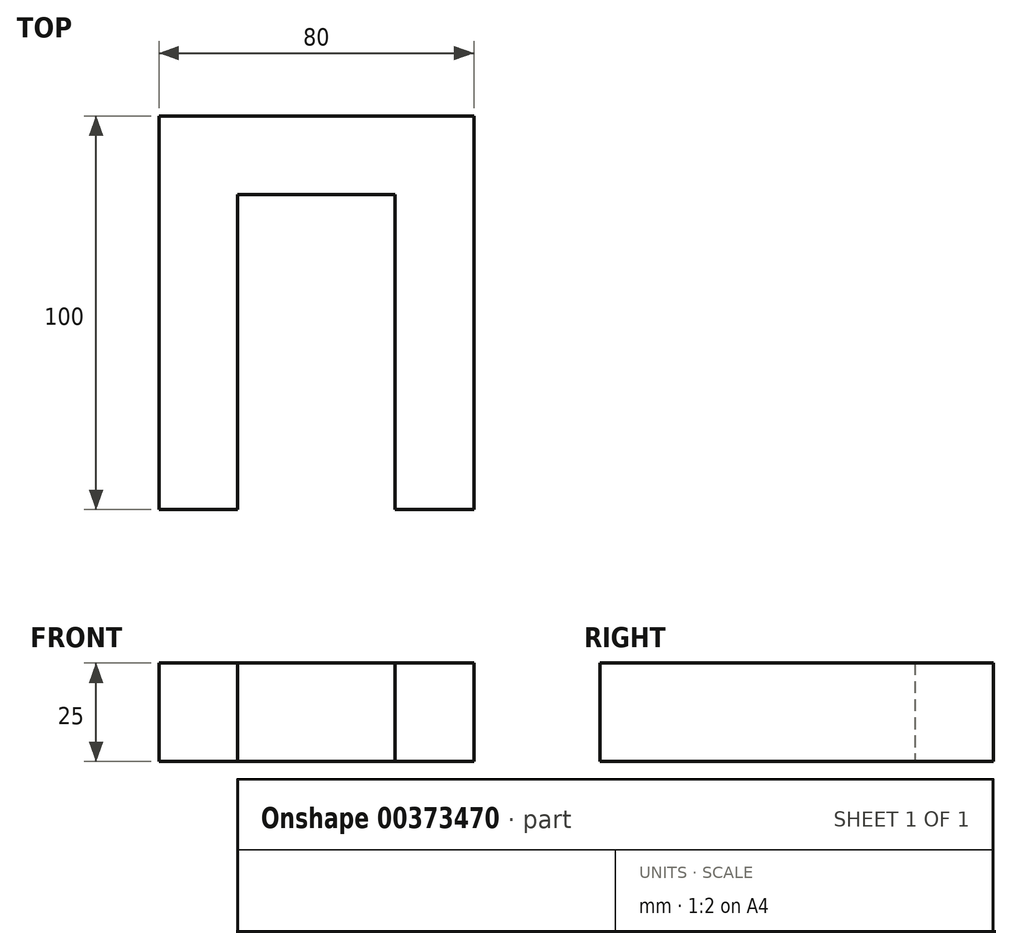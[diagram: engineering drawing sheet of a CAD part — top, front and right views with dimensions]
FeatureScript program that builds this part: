
annotation { "Feature Type Name" : "Feature", "Feature Type Description" : "" }
export const myFeature = defineFeature(function(context is Context, id is Id, definition is map)
    precondition{}
    {
        {
            var Q0;
            Q0=qCreatedBy(makeId("Top.planeOp"),FACE);
            var sketch = newSketch(context, id + "F0", { "sketchPlane" : qUnion([Q0])});
            skLineSegment(sketch, "E0.bottom", {"start": v(-80, -65.58) * mm, "end": v(-60, -65.58) * mm});
            skLineSegment(sketch, "E0.left", {"start": v(-80, -65.58) * mm, "end": v(-80, 14.42) * mm});
            skLineSegment(sketch, "E0.right", {"start": v(-60, -65.58) * mm, "end": v(-60, 14.42) * mm});
            skLineSegment(sketch, "E1.bottom", {"start": v(-20, -65.58) * mm, "end": v(0, -65.58) * mm});
            skLineSegment(sketch, "E1.left", {"start": v(-20, -65.58) * mm, "end": v(-20, 14.42) * mm});
            skLineSegment(sketch, "E1.right", {"start": v(0, -65.58) * mm, "end": v(0, 14.42) * mm});
            skLineSegment(sketch, "E2.bottom", {"start": v(-80, 34.42) * mm, "end": v(0, 34.42) * mm});
            skLineSegment(sketch, "E2.top", {"start": v(-60, 14.42) * mm, "end": v(-20, 14.42) * mm});
            skLineSegment(sketch, "E2.left", {"start": v(-80, 34.42) * mm, "end": v(-80, 14.42) * mm});
            skLineSegment(sketch, "E2.right", {"start": v(0, 34.42) * mm, "end": v(0, 14.42) * mm});
            skSolve(sketch);
        }
        {
            var Q0;
            Q0 = qSketchRegion(id + "F0", true);
            extrude(context, id + "F1", {"entities" : qUnion([Q0]), "depth" : 25 * mm});
        }
    });
